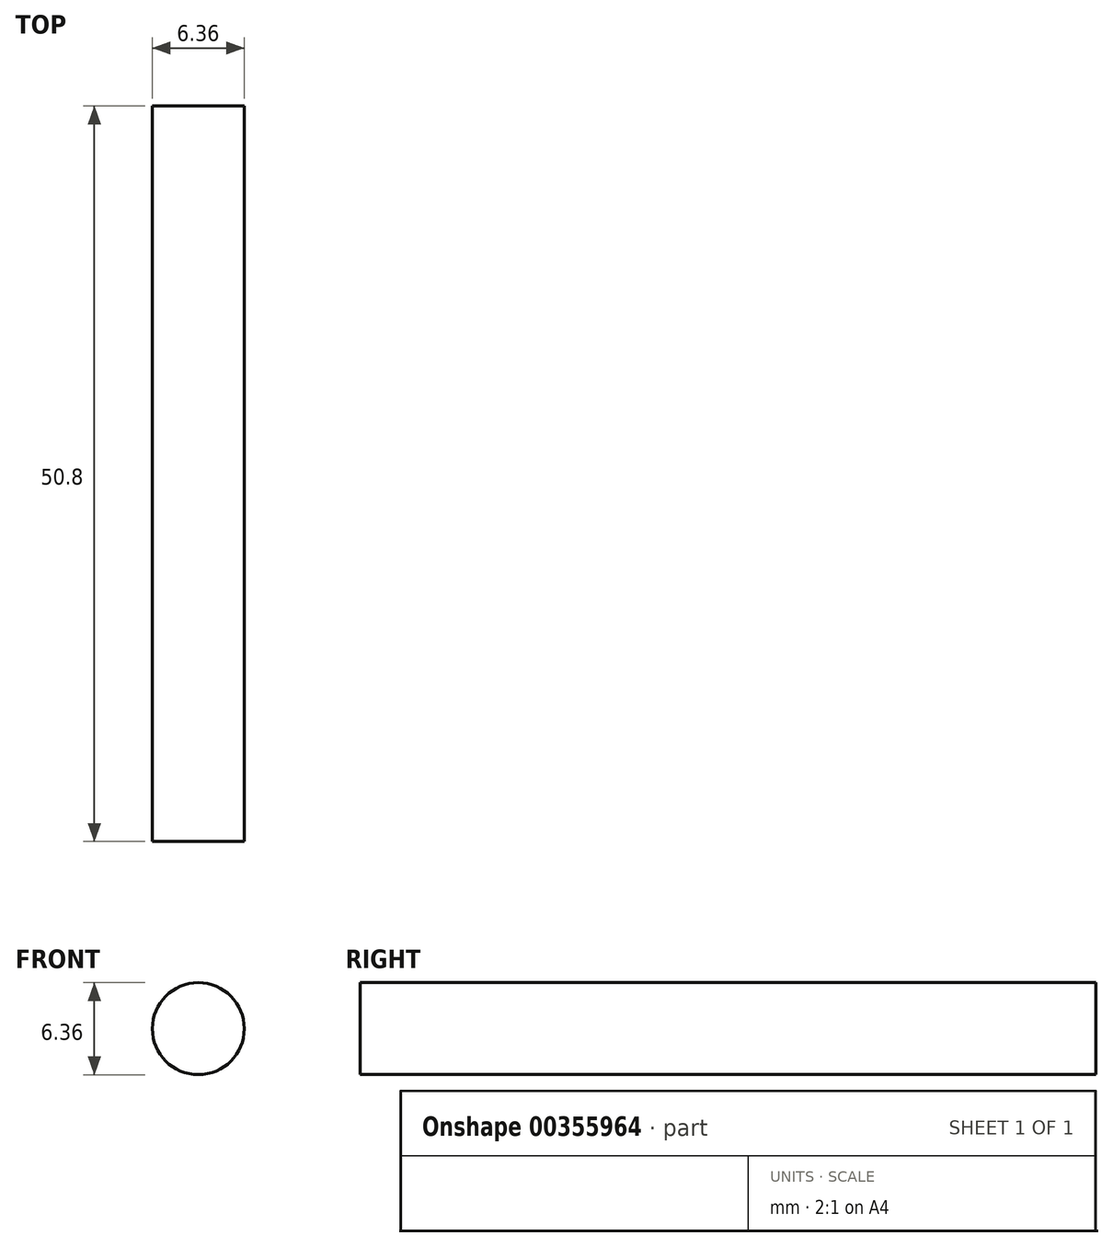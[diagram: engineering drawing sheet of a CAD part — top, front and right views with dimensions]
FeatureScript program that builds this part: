
annotation { "Feature Type Name" : "Feature", "Feature Type Description" : "" }
export const myFeature = defineFeature(function(context is Context, id is Id, definition is map)
    precondition{}
    {
        {
            var Q0;
            Q0=qCreatedBy(makeId("Front.planeOp"),FACE);
            var sketch = newSketch(context, id + "F0", { "sketchPlane" : qUnion([Q0])});
            skCircle(sketch, "E0", {"center": v(0, 0) * mm, "radius": 3.17 * mm});
            skSolve(sketch);
        }
        {
            var Q0;
            Q0=makeQuery(id+"F0.imprint","IMPRINT",FACE,{"disambiguationData":[TD([[makeQuery(id+"F0.imprint","IMPRINT",EDGE,{"derivedFrom":sQuery(id+"F0.wireOp",EDGE,"E0")}),1.0]])]});
            extrude(context, id + "F1", {"entities" : qUnion([Q0]), "depth" : 50.8 * mm});
        }
    });
